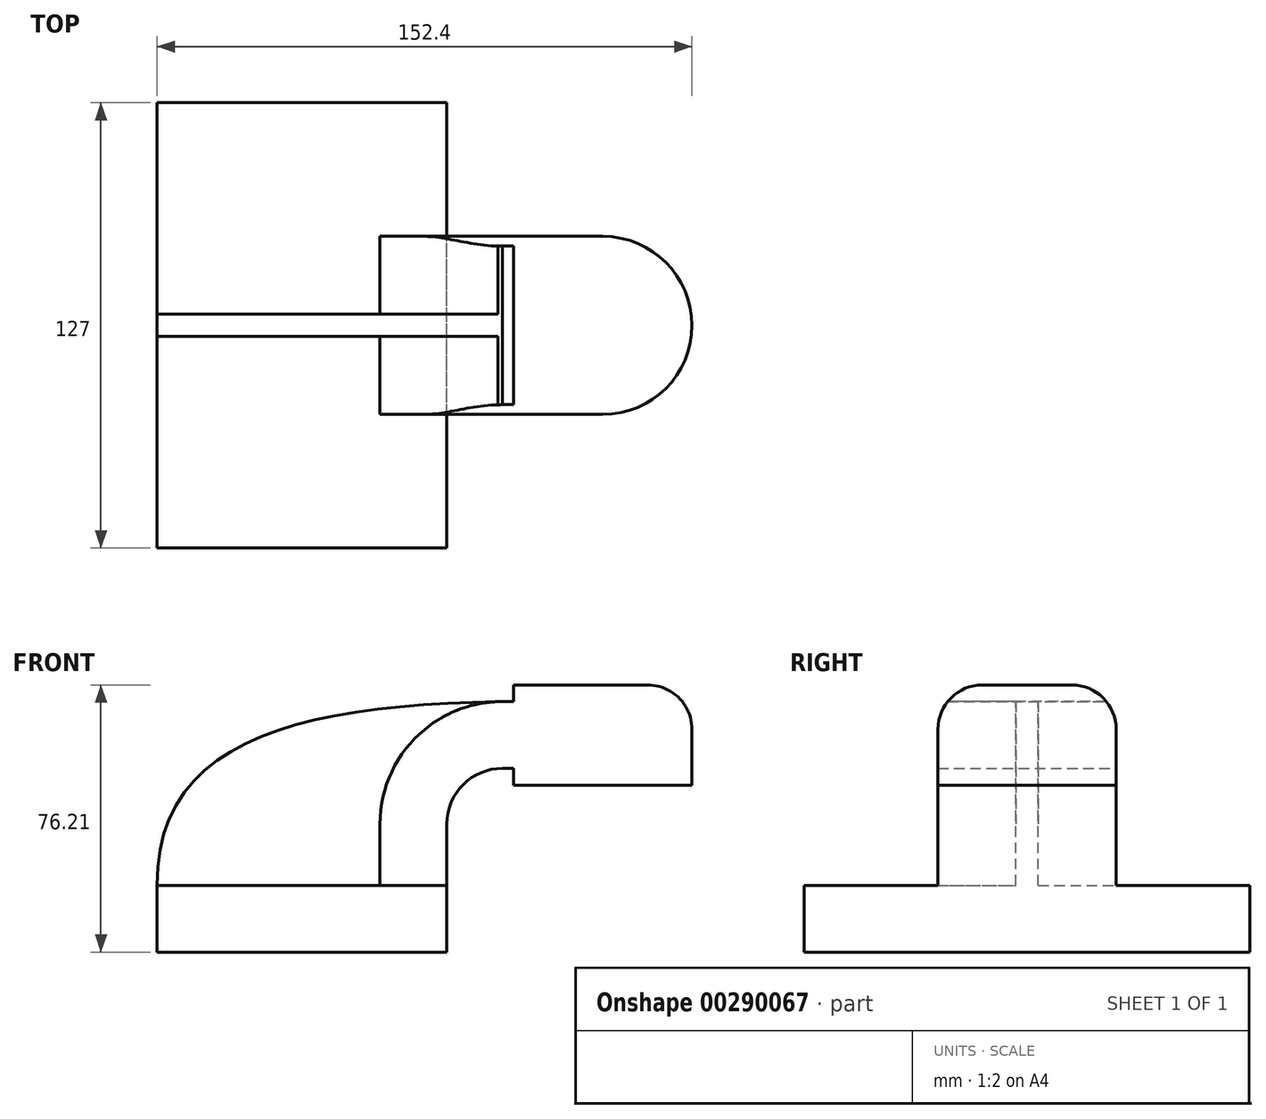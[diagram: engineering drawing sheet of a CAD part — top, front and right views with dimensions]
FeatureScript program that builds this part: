
annotation { "Feature Type Name" : "Feature", "Feature Type Description" : "" }
export const myFeature = defineFeature(function(context is Context, id is Id, definition is map)
    precondition{}
    {
        {
            var Q0;
            Q0=qCreatedBy(makeId("Front.planeOp"),FACE);
            var sketch = newSketch(context, id + "F0", { "sketchPlane" : qUnion([Q0])});
            skLineSegment(sketch, "E0.bottom", {"start": v(41.28, 9.52) * mm, "end": v(-41.28, 9.52) * mm});
            skLineSegment(sketch, "E0.top", {"start": v(41.28, -9.53) * mm, "end": v(-41.28, -9.53) * mm});
            skLineSegment(sketch, "E0.left", {"start": v(41.28, 9.52) * mm, "end": v(41.28, -9.53) * mm});
            skLineSegment(sketch, "E0.right", {"start": v(-41.28, 9.52) * mm, "end": v(-41.28, -9.53) * mm});
            skPoint(sketch, "E0.middle", {"position": v(0, 0) * mm});
            skLineSegment(sketch, "E1", {"start": v(41.28, 9.52) * mm, "end": v(41.28, 27) * mm});
            skArc(sketch, "E2", {"start": v(41.28, 27) * mm, "mid": v(45.92, 38.23) * mm, "end": v(57.15, 42.88) * mm});
            skLineSegment(sketch, "E3", {"start": v(57.15, 42.88) * mm, "end": v(85.72, 42.88) * mm});
            skLineSegment(sketch, "E4.bottom", {"start": v(111.12, 66.68) * mm, "end": v(60.32, 66.68) * mm});
            skLineSegment(sketch, "E4.top", {"start": v(111.12, 38.1) * mm, "end": v(60.32, 38.1) * mm});
            skLineSegment(sketch, "E4.left", {"start": v(111.12, 66.68) * mm, "end": v(111.12, 38.1) * mm});
            skLineSegment(sketch, "E4.right", {"start": v(60.32, 66.68) * mm, "end": v(60.32, 38.1) * mm});
            skPoint(sketch, "E4.middle", {"position": v(85.72, 52.39) * mm});
            skLineSegment(sketch, "E5.0", {"start": v(57.15, 61.93) * mm, "end": v(85.72, 61.93) * mm});
            skArc(sketch, "E5.1", {"start": v(22.23, 27) * mm, "mid": v(32.45, 51.7) * mm, "end": v(57.15, 61.93) * mm});
            skLineSegment(sketch, "E5.2", {"start": v(22.23, 9.52) * mm, "end": v(22.23, 27) * mm});
            skLineSegment(sketch, "E6", {"start": v(85.72, 38.1) * mm, "end": v(85.72, 66.68) * mm});
            skFitSpline(sketch, "E7", {"points": [v(-41.28, 9.52) * mm, v(57.15, 61.93) * mm], "startDerivative": vector(-0.95, 125.73) * mm, "endDerivative": vector(171.45, 2.9) * mm});
            skSolve(sketch);
        }
        {
            var Q0;
            Q0=makeQuery(id+"F0.imprint","IMPRINT",FACE,{"disambiguationData":[TD([[makeQuery(id+"F0.imprint","IMPRINT",EDGE,{"derivedFrom":sQuery(id+"F0.wireOp",EDGE,"E0.top")}),-1.0]])]});
            extrude(context, id + "F1", {"entities" : qUnion([Q0]), "endBound" : BoundingType.SYMMETRIC, "depth" : 127 * mm});
        }
        {
            var Q0;
            {var subQ9=sQuery(id+"F0.wireOp",EDGE,"E1");Q0=makeQuery(id+"F0.imprint","IMPRINT",FACE,{"disambiguationData":[TD([[makeQuery(id+"F0.imprint","IMPRINT",EDGE,{"derivedFrom":subQ9}),1.0]])]});}
            var Q1;
            {var subQ0=sQuery(id+"F0.wireOp",EDGE,"E6");var subQ1=sQuery(id+"F0.wireOp",EDGE,"E3");var subQ2=makeQuery(id+"F0.imprint","INTERSECT",VERTEX,{"derivedFrom":[subQ1,subQ0]});Q1=makeQuery(id+"F0.imprint","IMPRINT",FACE,{"disambiguationData":[TD([[makeQuery(id+"F0.imprint","IMPRINT",EDGE,{"disambiguationData":[TD([[subQ2,1.0]])],"derivedFrom":subQ1}),1.0]])]});}
            var Q2;
            {var subQ0=sQuery(id+"F0.wireOp",EDGE,"E4.right");var subQ1=sQuery(id+"F0.wireOp",EDGE,"E4.bottom");var subQ2=makeQuery(id+"F0.imprint","INTERSECT",VERTEX,{"derivedFrom":[subQ1,subQ0]});Q2=makeQuery(id+"F0.imprint","IMPRINT",FACE,{"disambiguationData":[TD([[makeQuery(id+"F0.imprint","IMPRINT",EDGE,{"disambiguationData":[TD([[subQ2,1.0]])],"derivedFrom":subQ1}),1.0]])]});}
            var Q3;
            {var subQ0=sQuery(id+"F0.wireOp",EDGE,"E6");var subQ1=sQuery(id+"F0.wireOp",EDGE,"E3");var subQ2=makeQuery(id+"F0.imprint","INTERSECT",VERTEX,{"derivedFrom":[subQ1,subQ0]});Q3=makeQuery(id+"F0.imprint","IMPRINT",FACE,{"disambiguationData":[TD([[makeQuery(id+"F0.imprint","IMPRINT",EDGE,{"disambiguationData":[TD([[subQ2,1.0]])],"derivedFrom":subQ1}),-1.0]])]});}
            extrude(context, id + "F2", {"entities" : qUnion([Q0, Q1, Q2, Q3]), "operationType" : NewBodyOperationType.ADD, "endBound" : BoundingType.SYMMETRIC, "depth" : 50.8 * mm});
        }
        {
            var Q0;
            {var subQ4=sQuery(id+"F0.wireOp",EDGE,"E4.left");Q0=makeQuery(id+"F0.imprint","IMPRINT",FACE,{"disambiguationData":[TD([[makeQuery(id+"F0.imprint","IMPRINT",EDGE,{"derivedFrom":subQ4}),-1.0]])]});}
            var Q1;
            Q1=sQuery(id+"F0.wireOp",EDGE,"E6");
            revolve(context, id + "F3", {"operationType" : NewBodyOperationType.ADD, "entities" : qUnion([Q0]), "axis" : qUnion([Q1]), "revolveType" : RevolveType.FULL});
        }
        {
            var Q0;
            {var subQ3=sQuery(id+"F0.wireOp",EDGE,"E5.2");Q0=makeQuery(id+"F0.imprint","IMPRINT",FACE,{"disambiguationData":[TD([[makeQuery(id+"F0.imprint","IMPRINT",EDGE,{"derivedFrom":subQ3}),1.0]])]});}
            extrude(context, id + "F4", {"entities" : qUnion([Q0]), "operationType" : NewBodyOperationType.ADD, "endBound" : BoundingType.SYMMETRIC, "depth" : 6.35 * mm});
        }
        {
            var Q0;
            Q0=makeQuery(id+"F3.opRevolve","SWEPT_EDGE",EDGE,{"disambiguationData":[OSD([sQuery(id+"F0.wireOp",EDGE,"E4.bottom"),sQuery(id+"F0.wireOp",EDGE,"E4.left")])]});
            fillet(context, id + "F5", {"entities" : qUnion([Q0]), "radius" : 12.7 * mm, "tangentPropagation" : true, "allowEdgeOverflow" : false});
        }
    });
